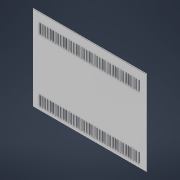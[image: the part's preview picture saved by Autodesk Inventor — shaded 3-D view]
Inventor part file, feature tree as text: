
AUTODESK INVENTOR PART (.ipt)
format: ipt  version: 2022 (Build 260153070, 153G)  size: 561,152 bytes
history: native  units: mm
features: chamfer x2, extrude x1, other x1, sketch x1
ambient origin geometry x8: Origin, YZ Plane, XZ Plane, XY Plane, X Axis, Y Axis, Z Axis, Center Point
bodies: Body1 (feature_tree)
feature tree (5):
  extrude  "Выдавливание2"  Depth=3.0mm
  chamfer  "Фаска1"  Distance=218.0mm
  chamfer  "Фаска2"  Distance=163.0mm
  other  "Определение главной стороны"
  sketch  "Эскиз2"
